# Revit family: Kessel 99706.30D en
name_source: partatom
category: Plumbing Fixtures
revit_build: Autodesk Revit Architecture 2014 (Build: 20130308_1515(x64)
units: mm (PartAtom-declared; Revit-internal decimal feet)

## types (1)
- Kessel 99706.30D en
    <1.010.00.2> Number of the part of the guideline = 98
    <1.010.00.3> Issue date (month) of the guideline = 200601
    <1.010.00.4> Manufacturer name = Kessel
    <1.010.00.5> Revision date of the file = 20190227
    <1.800.00.3> BS number = 002001000002007017019014019001004004006???03200004???
    <1.800.00.4> Comment field = EasyOil ground coalescence separator, NS 6, Class I, 4300 l, D
    <1.810.00.3> Manufacturer’s reference number = 99706.30D
    <1.810.00.4> DATANORM number = 99706.30D
    <1.810.00.6> GTIN number = 4026092027646
    <1.960/3L.00.8> Link (URL) = http://www.kessel.de
    <98.100.00.4> Area of application = Light liquid separator
    <98.110.00.4> Product series = EasyOil ground coalescence separator
    <98.200.00.3> Installation of the separators (DIN 19901) = Installation in the ground
    <98.250.00.3> Disposal variant = -
    <98.260.00.3> Sludge trap content (liters) = 2500
    <98.300.00.3> Separator content (liters) = -
    <98.350.00.3> Fat storage (liters) = -
    <98.360.00.3> Total volume (liters) = 4300
    <98.400.00.3> Layer thickness measurement (SonicControl) = no
    <98.450.00.3> Inlet nominal diameter (DN) = 200
    <98.460.00.3> Outlet nominal diameter (DN) = 200
    <98.500.00.3> Nominal size (NS) = 3
    <98.700.00.4> Product name = EasyOil ground coalescence separator, NS 6, Class I, 4300 l, D
    CONNECTOR0_DIAMETER_dX_0r = 0 mm  [stored 0 ft]
    CONNECTOR0_dX_00 = 1460 mm
    CONNECTOR0_dX_01 = 1410 mm
    CONNECTOR0_ref_dX = 1410 mm
    CONNECTOR0_ref_dZ = 820 mm
    CONNECTOR1_DIAMETER_dX_0r = 0 mm  [stored 0 ft]
    CONNECTOR1_dX_00 = 1410 mm
    CONNECTOR1_dX_01 = 1460 mm
    CONNECTOR1_ref_dX = 1410 mm
    CONNECTOR1_ref_dZ = 790 mm
    Manufacturer = Kessel
    Model = 99706.30D
    URL = www.kessel.com

note: [stored X ft] marks values corroborated as IEEE doubles in the binary element streams (Revit-internal decimal feet)
